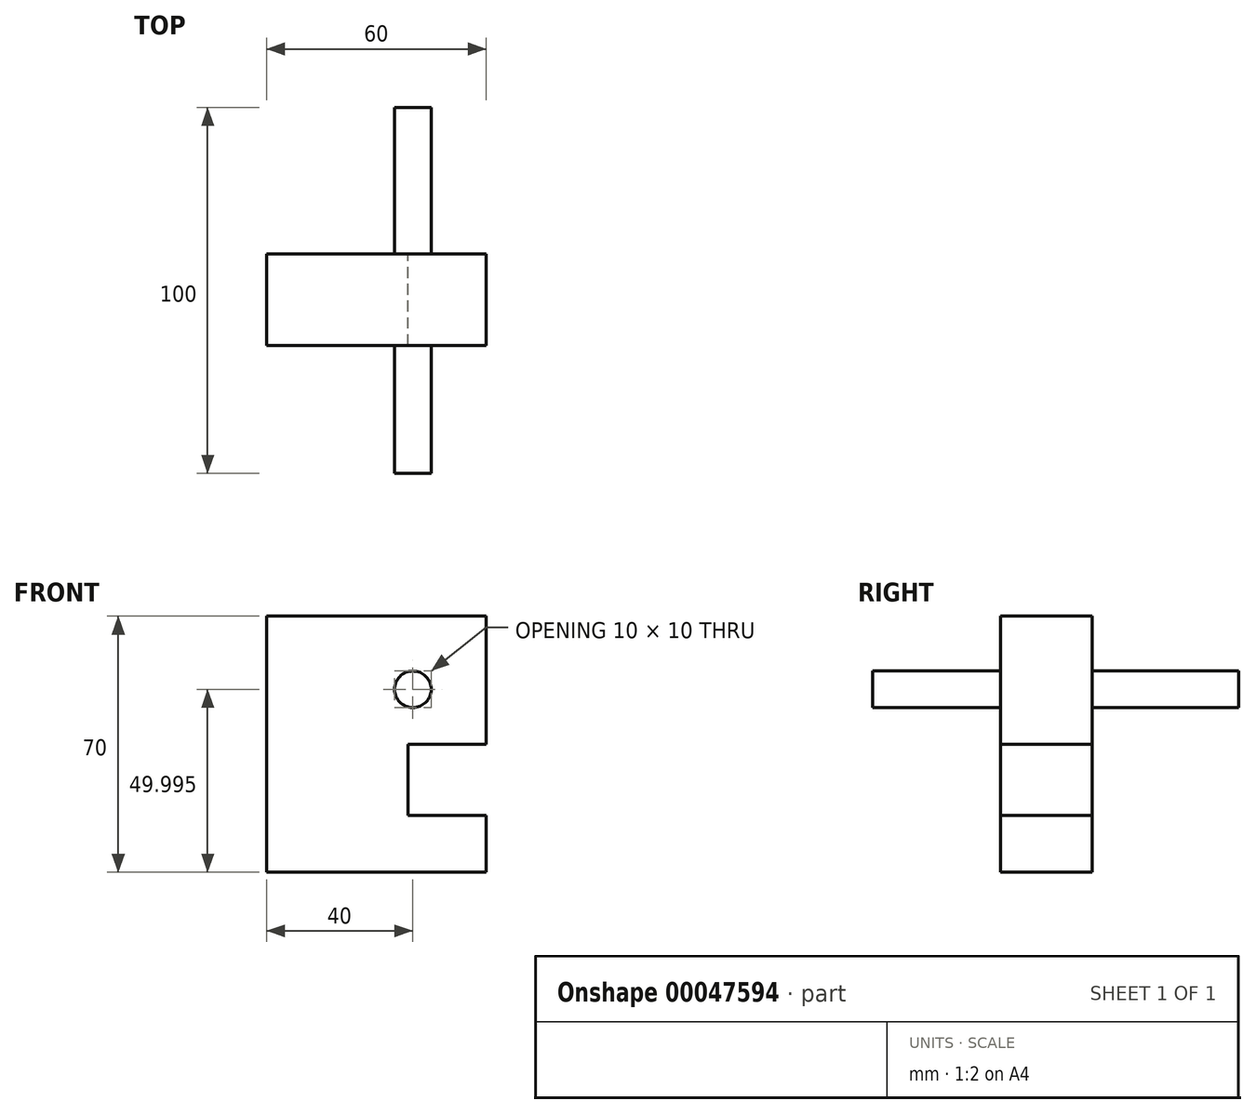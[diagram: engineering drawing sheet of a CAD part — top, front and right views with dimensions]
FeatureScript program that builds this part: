
annotation { "Feature Type Name" : "Feature", "Feature Type Description" : "" }
export const myFeature = defineFeature(function(context is Context, id is Id, definition is map)
    precondition{}
    {
        {
            var Q0;
            Q0=qCreatedBy(makeId("Front.planeOp"),FACE);
            var sketch = newSketch(context, id + "F0", { "sketchPlane" : qUnion([Q0])});
            skLineSegment(sketch, "E0.bottom", {"start": v(-60, 83.97) * mm, "end": v(0, 83.97) * mm});
            skLineSegment(sketch, "E0.top", {"start": v(-60, 13.97) * mm, "end": v(0, 13.97) * mm});
            skLineSegment(sketch, "E0.left", {"start": v(-60, 83.97) * mm, "end": v(-60, 13.97) * mm});
            skLineSegment(sketch, "E0.right", {"start": v(0, 83.97) * mm, "end": v(0, 13.97) * mm});
            skLineSegment(sketch, "E1.bottom", {"start": v(0, 48.97) * mm, "end": v(-21.4, 48.97) * mm});
            skLineSegment(sketch, "E1.top", {"start": v(0, 29.56) * mm, "end": v(-21.4, 29.56) * mm});
            skLineSegment(sketch, "E1.left", {"start": v(0, 48.97) * mm, "end": v(0, 29.56) * mm});
            skLineSegment(sketch, "E1.right", {"start": v(-21.4, 48.97) * mm, "end": v(-21.4, 29.56) * mm});
            skSolve(sketch);
        }
        {
            var Q0;
            {var subQ5=sQuery(id+"F0.wireOp",EDGE,"E0.bottom");Q0=makeQuery(id+"F0.imprint","IMPRINT",FACE,{"disambiguationData":[TD([[makeQuery(id+"F0.imprint","IMPRINT",EDGE,{"derivedFrom":subQ5}),-1.0]])]});}
            extrude(context, id + "F1", {"entities" : qUnion([Q0]), "depth" : 25 * mm});
        }
        {
            var Q0;
            Q0=makeQuery(id+"F1.opExtrude","CAP_FACE",FACE,{"disambiguationData":[OSD([sQuery(id+"F0.wireOp",EDGE,"E0.bottom"),sQuery(id+"F0.wireOp",EDGE,"E0.top"),sQuery(id+"F0.wireOp",EDGE,"E0.left"),sQuery(id+"F0.wireOp",EDGE,"E0.right"),sQuery(id+"F0.wireOp",EDGE,"E1.bottom"),sQuery(id+"F0.wireOp",EDGE,"E1.top"),sQuery(id+"F0.wireOp",EDGE,"E1.right")])],"isStart":true});
            var sketch = newSketch(context, id + "F2", { "sketchPlane" : qUnion([Q0])});
            skCircle(sketch, "E2", {"center": v(20, 63.97) * mm, "radius": 5 * mm});
            skSolve(sketch);
        }
        {
            var Q0;
            Q0 = qSketchRegion(id + "F2", true);
            extrude(context, id + "F3", {"entities" : qUnion([Q0]), "operationType" : NewBodyOperationType.ADD, "oppositeDirection" : true, "depth" : 60 * mm, "hasSecondDirection" : true, "secondDirectionOppositeDirection" : false, "secondDirectionDepth" : 40 * mm});
        }
    });
